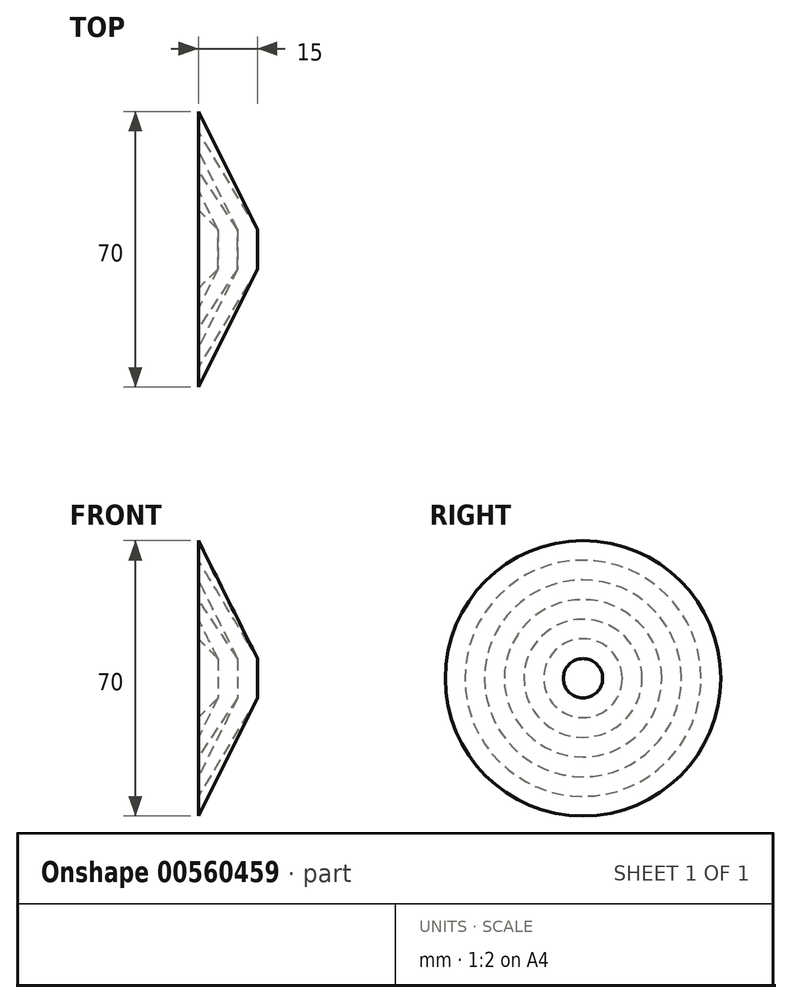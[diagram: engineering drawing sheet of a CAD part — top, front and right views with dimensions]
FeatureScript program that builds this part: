
annotation { "Feature Type Name" : "Feature", "Feature Type Description" : "" }
export const myFeature = defineFeature(function(context is Context, id is Id, definition is map)
    precondition{}
    {
        {
            var Q0;
            Q0=qCreatedBy(makeId("Top.planeOp"),FACE);
            var sketch = newSketch(context, id + "F0", { "sketchPlane" : qUnion([Q0])});
            skLineSegment(sketch, "E0", {"start": v(5, -5) * mm, "end": v(0, -10) * mm});
            skLineSegment(sketch, "E1", {"start": v(0, -10) * mm, "end": v(0, -15) * mm});
            skLineSegment(sketch, "E2", {"start": v(0, -15) * mm, "end": v(5, -5) * mm});
            skLineSegment(sketch, "E3", {"start": v(-14.23, 0) * mm, "end": v(10.78, 0) * mm, "construction": true});
            skLineSegment(sketch, "E4", {"start": v(0, -20) * mm, "end": v(10, -5) * mm});
            skLineSegment(sketch, "E5", {"start": v(10, -5) * mm, "end": v(0, -25) * mm});
            skLineSegment(sketch, "E6", {"start": v(0, -25) * mm, "end": v(0, -20) * mm});
            skLineSegment(sketch, "E7", {"start": v(0, -30) * mm, "end": v(15, -5) * mm});
            skLineSegment(sketch, "E8", {"start": v(15, -5) * mm, "end": v(0, -35) * mm});
            skLineSegment(sketch, "E9", {"start": v(0, -35) * mm, "end": v(0, -30) * mm});
            skSolve(sketch);
        }
        {
            var Q0;
            Q0=makeQuery(id+"F0.imprint","IMPRINT",FACE,{"disambiguationData":[TD([[makeQuery(id+"F0.imprint","IMPRINT",EDGE,{"derivedFrom":sQuery(id+"F0.wireOp",EDGE,"E0")}),1.0]])]});
            var Q1;
            Q1=makeQuery(id+"F0.imprint","IMPRINT",FACE,{"disambiguationData":[TD([[makeQuery(id+"F0.imprint","IMPRINT",EDGE,{"derivedFrom":sQuery(id+"F0.wireOp",EDGE,"E4")}),-1.0]])]});
            var Q2;
            Q2=makeQuery(id+"F0.imprint","IMPRINT",FACE,{"disambiguationData":[TD([[makeQuery(id+"F0.imprint","IMPRINT",EDGE,{"derivedFrom":sQuery(id+"F0.wireOp",EDGE,"E7")}),-1.0]])]});
            var Q3;
            Q3=sQuery(id+"F0.wireOp",EDGE,"E3");
            var Q4;
            Q4=sQuery(id+"F0.wireOp",EDGE,"E3");
            revolve(context, id + "F1", {"entities" : qUnion([Q0, Q1, Q2]), "surfaceEntities" : qUnion([Q3]), "axis" : qUnion([Q4]), "revolveType" : RevolveType.FULL});
        }
    });
